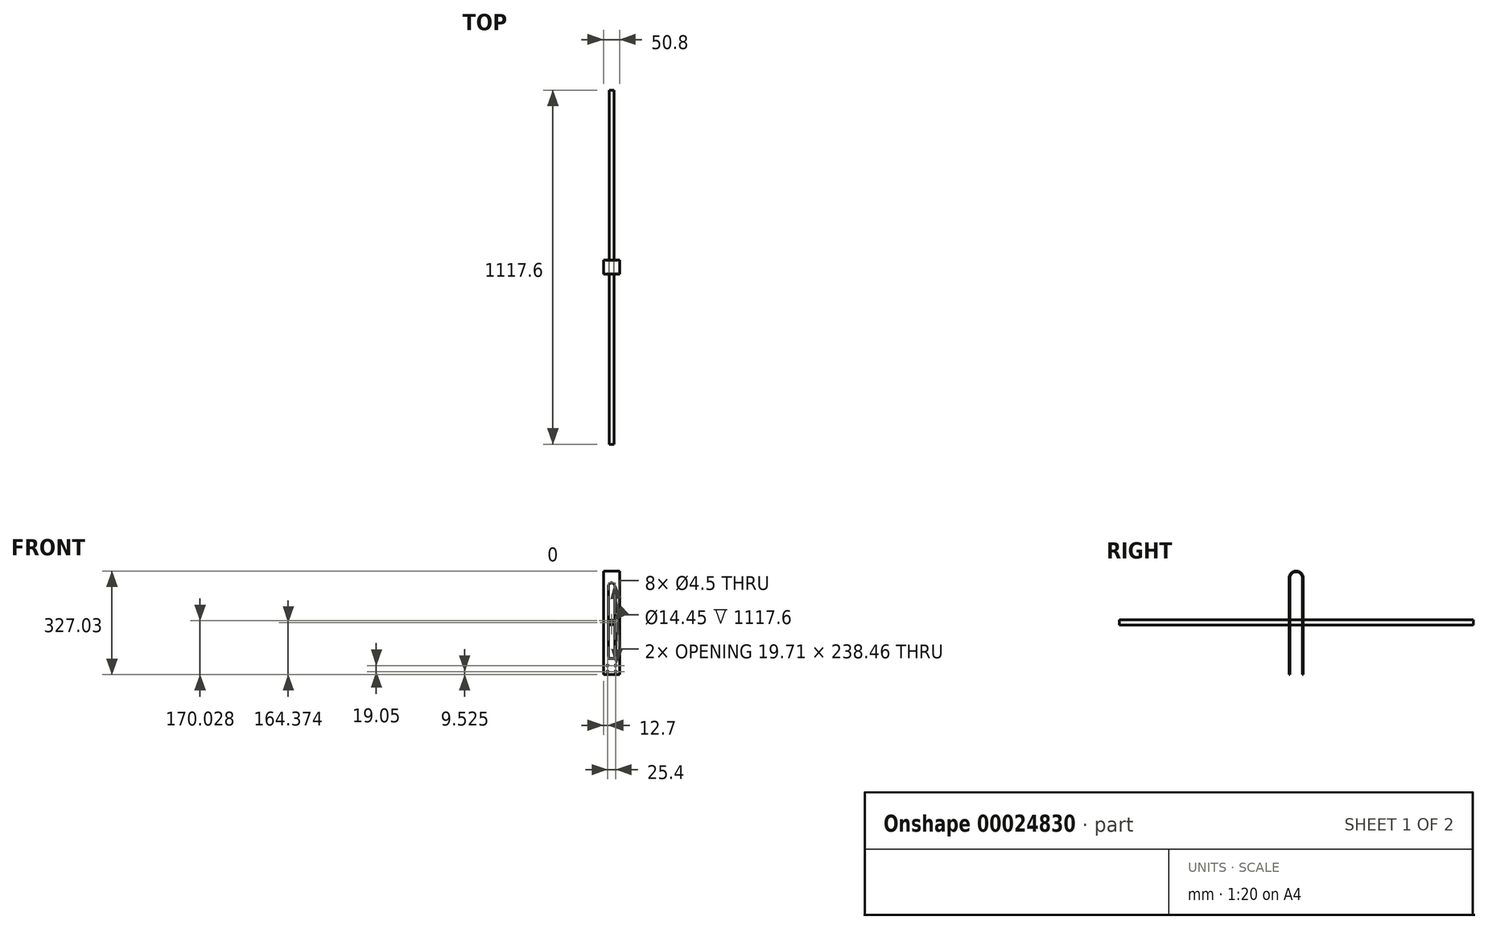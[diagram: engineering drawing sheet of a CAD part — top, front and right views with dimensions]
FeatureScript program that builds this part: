
annotation { "Feature Type Name" : "Feature", "Feature Type Description" : "" }
export const myFeature = defineFeature(function(context is Context, id is Id, definition is map)
    precondition{}
    {
        {
            var Q0;
            Q0=qCreatedBy(makeId("Right.planeOp"),FACE);
            var sketch = newSketch(context, id + "F0", { "sketchPlane" : qUnion([Q0])});
            skLineSegment(sketch, "E0.bottom", {"start": v(-19.69, 0) * mm, "end": v(19.68, 0) * mm});
            skLineSegment(sketch, "E0.top", {"start": v(-19.69, 304.8) * mm, "end": v(19.68, 304.8) * mm});
            skLineSegment(sketch, "E0.left", {"start": v(-19.69, 0) * mm, "end": v(-19.69, 304.8) * mm});
            skLineSegment(sketch, "E0.right", {"start": v(19.68, 0) * mm, "end": v(19.68, 304.8) * mm});
            skPoint(sketch, "E1", {"position": v(0, 0) * mm});
            skArc(sketch, "E2", {"start": v(19.68, 304.8) * mm, "mid": v(0, 324.49) * mm, "end": v(-19.69, 304.8) * mm});
            skLineSegment(sketch, "E3.0", {"start": v(22.22, 0) * mm, "end": v(22.22, 304.8) * mm});
            skArc(sketch, "E3.1", {"start": v(22.22, 304.8) * mm, "mid": v(0, 327.03) * mm, "end": v(-22.23, 304.8) * mm});
            skLineSegment(sketch, "E3.2", {"start": v(-22.23, 0) * mm, "end": v(-22.23, 304.8) * mm});
            skLineSegment(sketch, "E4", {"start": v(-19.69, 0) * mm, "end": v(-22.23, 0) * mm});
            skLineSegment(sketch, "E5", {"start": v(19.68, 0) * mm, "end": v(22.22, 0) * mm});
            skSolve(sketch);
        }
        {
            var Q0;
            Q0=makeQuery(id+"F0.imprint","IMPRINT",FACE,{"disambiguationData":[TD([[makeQuery(id+"F0.imprint","IMPRINT",EDGE,{"derivedFrom":sQuery(id+"F0.wireOp",EDGE,"E0.left")}),1.0]])]});
            extrude(context, id + "F1", {"entities" : qUnion([Q0]), "endBound" : BoundingType.SYMMETRIC, "depth" : 50.8 * mm});
        }
        {
            var Q0;
            Q0=qCreatedBy(makeId("Front.planeOp"),FACE);
            var sketch = newSketch(context, id + "F2", { "sketchPlane" : qUnion([Q0])});
            skLineSegment(sketch, "E6.rect.bottom", {"start": v(-9.86, 279.4) * mm, "end": v(9.86, 279.4) * mm});
            skLineSegment(sketch, "E6.rect.top", {"start": v(-9.86, 50.8) * mm, "end": v(9.86, 50.8) * mm});
            skLineSegment(sketch, "E6.rect.left", {"start": v(-9.86, 279.4) * mm, "end": v(-9.86, 50.8) * mm});
            skLineSegment(sketch, "E6.rect.right", {"start": v(9.86, 279.4) * mm, "end": v(9.86, 50.8) * mm});
            skPoint(sketch, "E6.rect.middle", {"position": v(0, 165.1) * mm});
            skCircle(sketch, "E7", {"center": v(0, 279.4) * mm, "radius": 9.86 * mm});
            skCircle(sketch, "E8", {"center": v(0, 50.8) * mm, "radius": 9.86 * mm});
            skLineSegment(sketch, "E9.rect.bottom", {"start": v(-12.7, 28.58) * mm, "end": v(12.7, 28.58) * mm, "construction": true});
            skLineSegment(sketch, "E9.rect.top", {"start": v(-12.7, 9.53) * mm, "end": v(12.7, 9.53) * mm, "construction": true});
            skLineSegment(sketch, "E9.rect.left", {"start": v(-12.7, 28.58) * mm, "end": v(-12.7, 9.53) * mm, "construction": true});
            skLineSegment(sketch, "E9.rect.right", {"start": v(12.7, 28.58) * mm, "end": v(12.7, 9.53) * mm, "construction": true});
            skPoint(sketch, "E9.rect.middle", {"position": v(0, 19.05) * mm});
            skCircle(sketch, "E10", {"center": v(-12.7, 28.58) * mm, "radius": 2.25 * mm});
            skCircle(sketch, "E11", {"center": v(12.7, 28.58) * mm, "radius": 2.25 * mm});
            skCircle(sketch, "E12", {"center": v(-12.7, 9.53) * mm, "radius": 2.25 * mm});
            skCircle(sketch, "E13", {"center": v(12.7, 9.53) * mm, "radius": 2.25 * mm});
            skSolve(sketch);
        }
        {
            var Q0;
            {var subQ3=sQuery(id+"F2.wireOp",EDGE,"E6.rect.left");Q0=makeQuery(id+"F2.imprint","IMPRINT",FACE,{"disambiguationData":[TD([[makeQuery(id+"F2.imprint","IMPRINT",EDGE,{"derivedFrom":subQ3}),1.0]])]});}
            var Q1;
            {var subQ1=sQuery(id+"F2.wireOp",EDGE,"E6.rect.bottom");Q1=makeQuery(id+"F2.imprint","IMPRINT",FACE,{"disambiguationData":[TD([[makeQuery(id+"F2.imprint","IMPRINT",EDGE,{"derivedFrom":subQ1}),-1.0]])]});}
            var Q2;
            {var subQ1=sQuery(id+"F2.wireOp",EDGE,"E6.rect.bottom");Q2=makeQuery(id+"F2.imprint","IMPRINT",FACE,{"disambiguationData":[TD([[makeQuery(id+"F2.imprint","IMPRINT",EDGE,{"derivedFrom":subQ1}),1.0]])]});}
            var Q3;
            {var subQ1=sQuery(id+"F2.wireOp",EDGE,"E6.rect.top");Q3=makeQuery(id+"F2.imprint","IMPRINT",FACE,{"disambiguationData":[TD([[makeQuery(id+"F2.imprint","IMPRINT",EDGE,{"derivedFrom":subQ1}),1.0]])]});}
            var Q4;
            Q4=makeQuery(id+"F2.imprint","IMPRINT",FACE,{"disambiguationData":[TD([[makeQuery(id+"F2.imprint","IMPRINT",EDGE,{"derivedFrom":sQuery(id+"F2.wireOp",EDGE,"E11")}),1.0]])]});
            var Q5;
            Q5=makeQuery(id+"F2.imprint","IMPRINT",FACE,{"disambiguationData":[TD([[makeQuery(id+"F2.imprint","IMPRINT",EDGE,{"derivedFrom":sQuery(id+"F2.wireOp",EDGE,"E13")}),1.0]])]});
            var Q6;
            Q6=makeQuery(id+"F2.imprint","IMPRINT",FACE,{"disambiguationData":[TD([[makeQuery(id+"F2.imprint","IMPRINT",EDGE,{"derivedFrom":sQuery(id+"F2.wireOp",EDGE,"E10")}),1.0]])]});
            var Q7;
            Q7=makeQuery(id+"F2.imprint","IMPRINT",FACE,{"disambiguationData":[TD([[makeQuery(id+"F2.imprint","IMPRINT",EDGE,{"derivedFrom":sQuery(id+"F2.wireOp",EDGE,"E12")}),1.0]])]});
            extrude(context, id + "F3", {"entities" : qUnion([Q0, Q1, Q2, Q3, Q4, Q5, Q6, Q7]), "operationType" : NewBodyOperationType.REMOVE, "endBound" : BoundingType.THROUGH_ALL, "oppositeDirection" : true, "depth" : 25.4 * mm, "hasSecondDirection" : true, "secondDirectionBound" : SecondDirectionBoundingType.THROUGH_ALL, "secondDirectionOppositeDirection" : false, "secondDirectionDepth" : 25.4 * mm});
        }
        {
            var Q0;
            Q0=qCreatedBy(makeId("Front.planeOp"),FACE);
            var sketch = newSketch(context, id + "F4", { "sketchPlane" : qUnion([Q0])});
            skCircle(sketch, "E14", {"center": v(0, 164.37) * mm, "radius": 7.94 * mm});
            skCircle(sketch, "E15", {"center": v(0, 164.37) * mm, "radius": 7.23 * mm});
            skSolve(sketch);
        }
        {
            var Q0;
            Q0=makeQuery(id+"F4.imprint","IMPRINT",FACE,{"disambiguationData":[TD([[makeQuery(id+"F4.imprint","IMPRINT",EDGE,{"derivedFrom":sQuery(id+"F4.wireOp",EDGE,"E14")}),1.0]])]});
            extrude(context, id + "F5", {"entities" : qUnion([Q0]), "endBound" : BoundingType.SYMMETRIC, "depth" : 1117.6 * mm});
        }
    });
